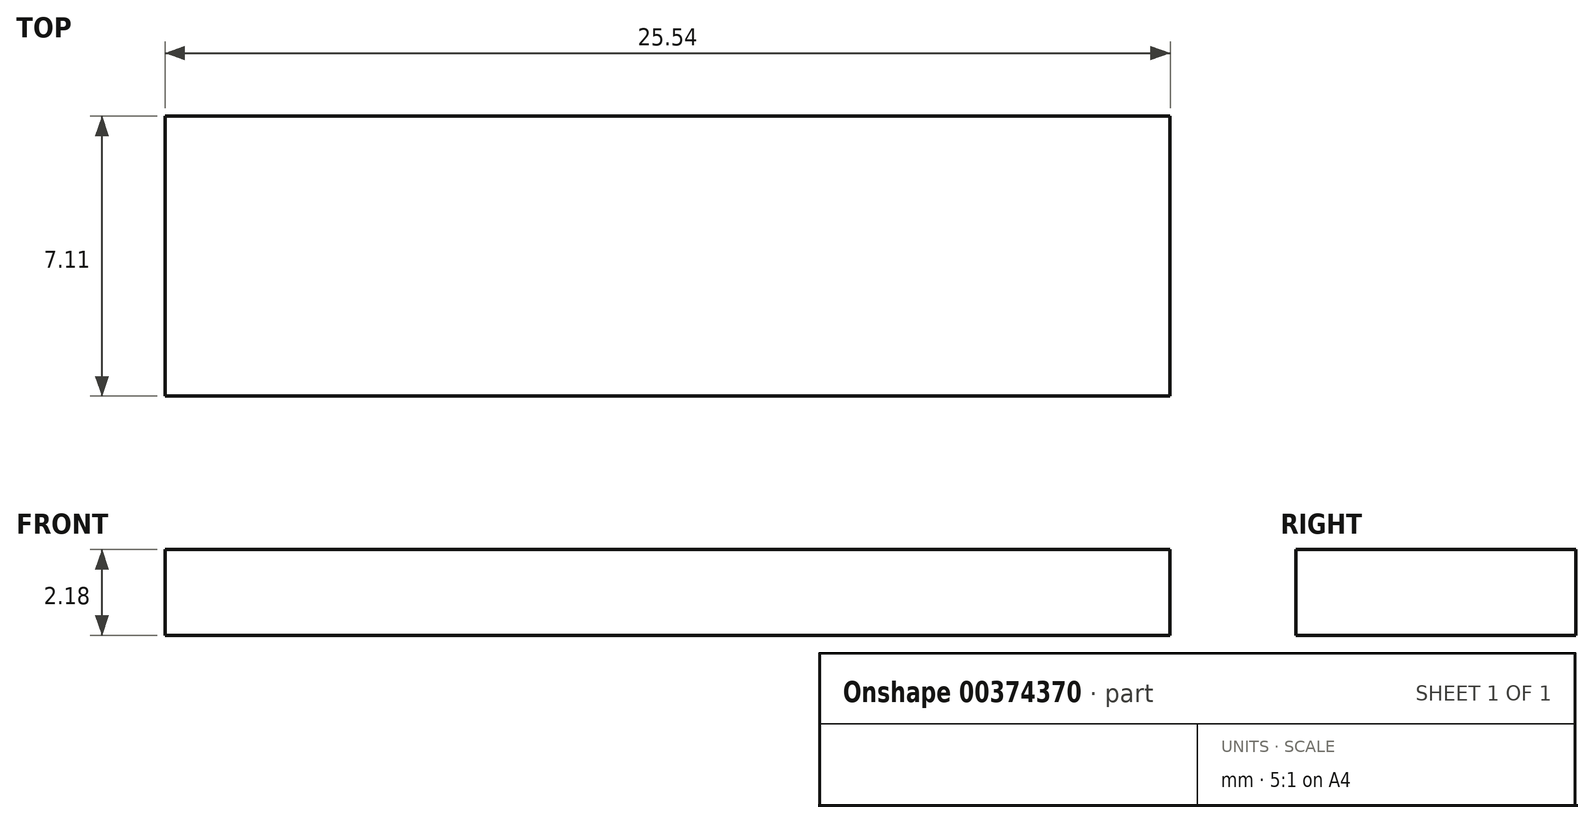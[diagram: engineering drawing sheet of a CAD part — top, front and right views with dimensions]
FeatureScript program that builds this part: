
annotation { "Feature Type Name" : "Feature", "Feature Type Description" : "" }
export const myFeature = defineFeature(function(context is Context, id is Id, definition is map)
    precondition{}
    {
        {
            var Q0;
            Q0=qCreatedBy(makeId("Front.planeOp"),FACE);
            var sketch = newSketch(context, id + "F0", { "sketchPlane" : qUnion([Q0])});
            skLineSegment(sketch, "E0.bottom", {"start": v(12.77, 1.1) * mm, "end": v(-12.77, 1.1) * mm});
            skLineSegment(sketch, "E0.top", {"start": v(12.77, -1.1) * mm, "end": v(-12.77, -1.1) * mm});
            skLineSegment(sketch, "E0.left", {"start": v(12.77, 1.1) * mm, "end": v(12.77, -1.1) * mm});
            skLineSegment(sketch, "E0.right", {"start": v(-12.77, 1.1) * mm, "end": v(-12.77, -1.1) * mm});
            skPoint(sketch, "E0.middle", {"position": v(0, 0) * mm});
            skSolve(sketch);
        }
        {
            var Q0;
            Q0=makeQuery(id+"F0.imprint","IMPRINT",FACE,{"disambiguationData":[TD([[makeQuery(id+"F0.imprint","IMPRINT",EDGE,{"derivedFrom":sQuery(id+"F0.wireOp",EDGE,"E0.bottom")}),1.0]])]});
            extrude(context, id + "F1", {"entities" : qUnion([Q0]), "depth" : 7.11 * mm});
        }
    });
